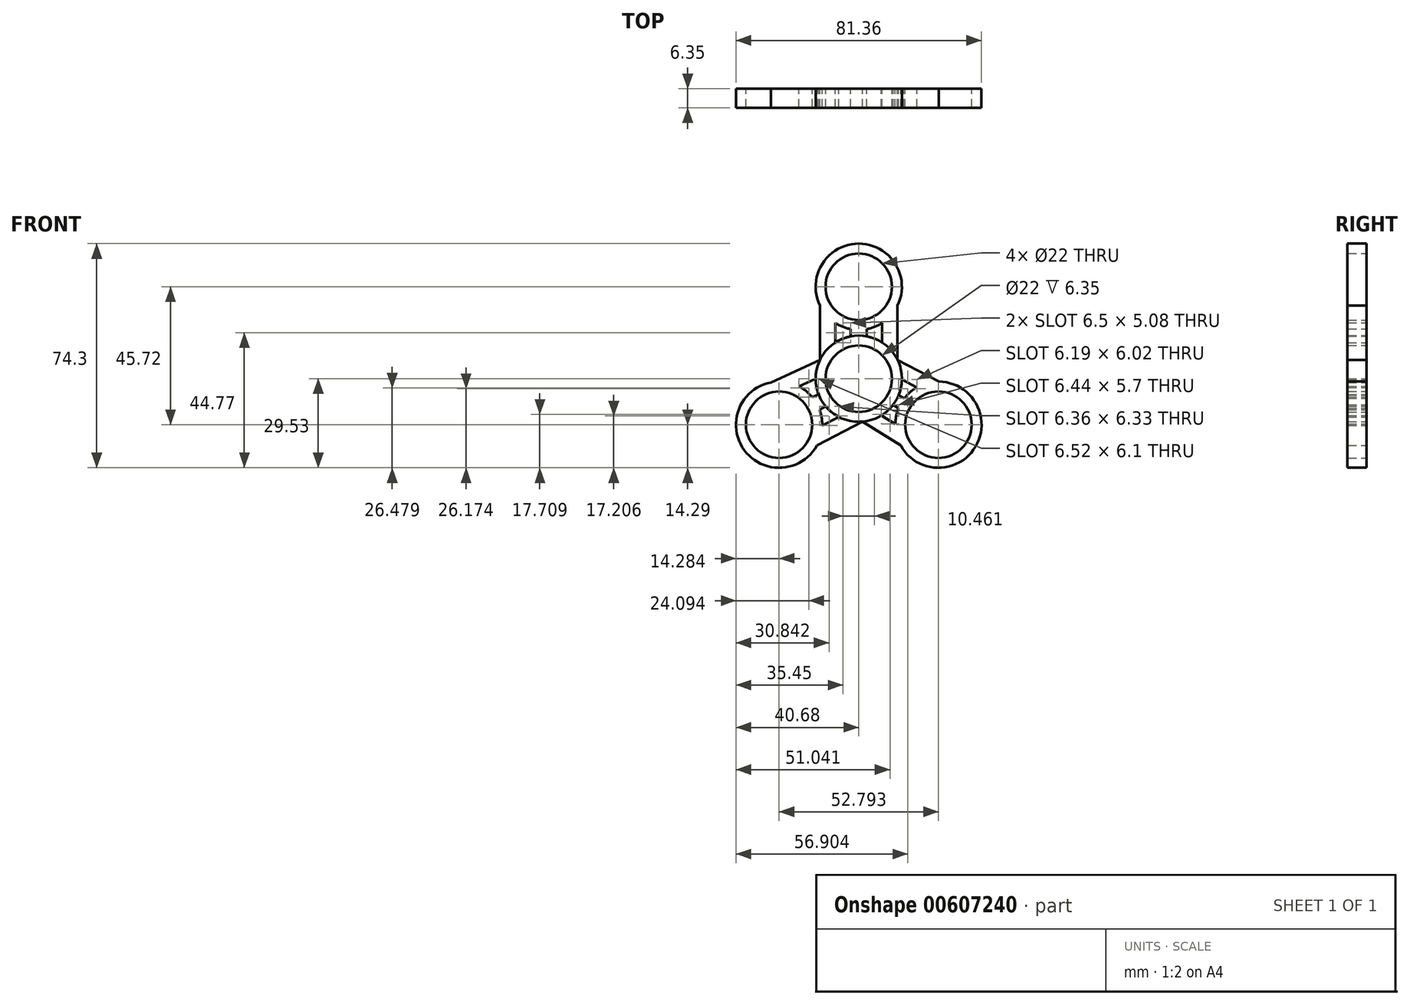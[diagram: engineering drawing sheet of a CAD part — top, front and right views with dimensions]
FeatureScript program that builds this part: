
annotation { "Feature Type Name" : "Feature", "Feature Type Description" : "" }
export const myFeature = defineFeature(function(context is Context, id is Id, definition is map)
    precondition{}
    {
        {
            var Q0;
            Q0=qCreatedBy(makeId("Front.planeOp"),FACE);
            var sketch = newSketch(context, id + "F0", { "sketchPlane" : qUnion([Q0])});
            skCircle(sketch, "E0", {"center": v(0, 0) * mm, "radius": 14.29 * mm});
            skCircle(sketch, "E1", {"center": v(0, 0) * mm, "radius": 11 * mm});
            skCircle(sketch, "E2", {"center": v(0, 30.48) * mm, "radius": 14.29 * mm});
            skCircle(sketch, "E3", {"center": v(0, 30.48) * mm, "radius": 11 * mm});
            skCircle(sketch, "E4.1.2", {"center": v(-26.4, -15.24) * mm, "radius": 11 * mm});
            skCircle(sketch, "E4.1.3", {"center": v(-26.4, -15.24) * mm, "radius": 14.29 * mm});
            skCircle(sketch, "E4.2.2", {"center": v(26.4, -15.24) * mm, "radius": 11 * mm});
            skCircle(sketch, "E4.2.3", {"center": v(26.4, -15.24) * mm, "radius": 14.29 * mm});
            skSolve(sketch);
        }
        {
            var Q0;
            Q0=qCreatedBy(makeId("Front.planeOp"),FACE);
            var sketch = newSketch(context, id + "F1", { "sketchPlane" : qUnion([Q0])});
            skCircle(sketch, "E5.0", {"center": v(0, 30.48) * mm, "radius": 14.29 * mm});
            skCircle(sketch, "E6.0", {"center": v(0, 30.48) * mm, "radius": 11 * mm});
            skCircle(sketch, "E7.0", {"center": v(0, 0) * mm, "radius": 11 * mm});
            skCircle(sketch, "E8.0", {"center": v(0, 0) * mm, "radius": 14.29 * mm});
            skCircle(sketch, "E9.0", {"center": v(26.4, -15.24) * mm, "radius": 11 * mm});
            skCircle(sketch, "E10.0", {"center": v(26.4, -15.24) * mm, "radius": 14.29 * mm});
            skCircle(sketch, "E11.0", {"center": v(-26.4, -15.24) * mm, "radius": 11 * mm});
            skCircle(sketch, "E12.0", {"center": v(-26.4, -15.24) * mm, "radius": 14.29 * mm});
            skLineSegment(sketch, "E13", {"start": v(-12.85, 24.24) * mm, "end": v(-12.85, 6.24) * mm});
            skLineSegment(sketch, "E14", {"start": v(12.85, 24.24) * mm, "end": v(12.85, 6.24) * mm});
            skLineSegment(sketch, "E15", {"start": v(-13.9, -22.15) * mm, "end": v(1.26, -14.23) * mm});
            skLineSegment(sketch, "E16", {"start": v(1.26, -14.23) * mm, "end": v(13.9, -22.15) * mm});
            skLineSegment(sketch, "E17", {"start": v(26.47, -0.95) * mm, "end": v(12.85, 6.24) * mm});
            skLineSegment(sketch, "E18", {"start": v(-12.85, 6.24) * mm, "end": v(-29.16, -1.22) * mm});
            skLineSegment(sketch, "E19", {"start": v(7.77, 11.99) * mm, "end": v(7.77, 18.5) * mm});
            skLineSegment(sketch, "E20", {"start": v(-7.77, 18.5) * mm, "end": v(-7.77, 11.99) * mm});
            skLineSegment(sketch, "E21", {"start": v(-14.29, 0) * mm, "end": v(-19.84, -2.54) * mm});
            skLineSegment(sketch, "E22", {"start": v(-12.11, -15.49) * mm, "end": v(-6.66, -12.64) * mm});
            skLineSegment(sketch, "E23", {"start": v(7.5, -12.16) * mm, "end": v(12.11, -15.04) * mm});
            skLineSegment(sketch, "E24", {"start": v(14.29, -0.26) * mm, "end": v(19.24, -2.88) * mm});
            skLineSegment(sketch, "E25", {"start": v(11.4, -8.6) * mm, "end": v(13.21, -9.73) * mm});
            skLineSegment(sketch, "E26", {"start": v(13.21, -5.44) * mm, "end": v(15.13, -6.45) * mm});
            skLineSegment(sketch, "E27", {"start": v(-13.33, -5.15) * mm, "end": v(-15.41, -6.1) * mm});
            skLineSegment(sketch, "E28", {"start": v(-13.02, -10.23) * mm, "end": v(-10.97, -9.16) * mm});
            skLineSegment(sketch, "E29", {"start": v(-10.97, -9.16) * mm, "end": v(-11.16, -9.28) * mm});
            skLineSegment(sketch, "E30", {"start": v(-2.7, 16.45) * mm, "end": v(-2.7, 14.03) * mm});
            skLineSegment(sketch, "E31", {"start": v(2.7, 16.45) * mm, "end": v(2.7, 14.03) * mm});
            skSolve(sketch);
        }
        {
            var Q0;
            {var subQ0=sQuery(id+"F1.wireOp",EDGE,"E8.0");var subQ1=sQuery(id+"F1.wireOp",EDGE,"E75473pT-KR4w-GPLl-tIWS-s1hwGxaYuD1d");var subQ2=makeQuery(id+"F1.imprint","INTERSECT",VERTEX,{"disambiguationData":[OD(0.0)],"derivedFrom":[subQ1,subQ0]});Q0=makeQuery(id+"F1.imprint","IMPRINT",FACE,{"disambiguationData":[TD([[makeQuery(id+"F1.imprint","IMPRINT",EDGE,{"disambiguationData":[TD([[subQ2,-1.0]])],"derivedFrom":subQ1}),1.0]])]});}
            var Q1;
            {var subQ0=sQuery(id+"F1.wireOp",EDGE,"E8.0");var subQ1=sQuery(id+"F1.wireOp",EDGE,"UQbH4uQf-tco6-kiW7-QBOc-czMYGTiRIqUf");var subQ2=makeQuery(id+"F1.imprint","INTERSECT",VERTEX,{"disambiguationData":[OD(0.0)],"derivedFrom":[subQ1,subQ0]});Q1=makeQuery(id+"F1.imprint","IMPRINT",FACE,{"disambiguationData":[TD([[makeQuery(id+"F1.imprint","IMPRINT",EDGE,{"disambiguationData":[TD([[subQ2,-1.0]])],"derivedFrom":subQ1}),1.0]])]});}
            var Q2;
            {var subQ0=sQuery(id+"F1.wireOp",EDGE,"RHKiTu8T-B7F3-O5vr-oPhw-GQMkx3ZWOzNJ");var subQ1=sQuery(id+"F1.wireOp",EDGE,"E5.0");var subQ2=makeQuery(id+"F1.imprint","INTERSECT",VERTEX,{"disambiguationData":[OD(0.0)],"derivedFrom":[subQ1,subQ0]});Q2=makeQuery(id+"F1.imprint","IMPRINT",FACE,{"disambiguationData":[TD([[makeQuery(id+"F1.imprint","IMPRINT",EDGE,{"disambiguationData":[TD([[subQ2,1.0]])],"derivedFrom":subQ1}),1.0]])]});}
            var Q3;
            {var subQ0=sQuery(id+"F1.wireOp",EDGE,"RHKiTu8T-B7F3-O5vr-oPhw-GQMkx3ZWOzNJ");var subQ1=sQuery(id+"F1.wireOp",EDGE,"E10.0");var subQ2=makeQuery(id+"F1.imprint","INTERSECT",VERTEX,{"disambiguationData":[OD(0.0)],"derivedFrom":[subQ1,subQ0]});Q3=makeQuery(id+"F1.imprint","IMPRINT",FACE,{"disambiguationData":[TD([[makeQuery(id+"F1.imprint","IMPRINT",EDGE,{"disambiguationData":[TD([[subQ2,-1.0]])],"derivedFrom":subQ1}),1.0]])]});}
            var Q4;
            Q4=makeQuery(id+"F1.imprint","IMPRINT",FACE,{"disambiguationData":[TD([[makeQuery(id+"F1.imprint","IMPRINT",EDGE,{"derivedFrom":sQuery(id+"F1.wireOp",EDGE,"E11.0")}),-1.0]])]});
            var Q5;
            Q5=makeQuery(id+"F1.imprint","IMPRINT",FACE,{"disambiguationData":[TD([[makeQuery(id+"F1.imprint","IMPRINT",EDGE,{"derivedFrom":sQuery(id+"F1.wireOp",EDGE,"E6.0")}),-1.0]])]});
            var Q6;
            Q6=makeQuery(id+"F1.imprint","IMPRINT",FACE,{"disambiguationData":[TD([[makeQuery(id+"F1.imprint","IMPRINT",EDGE,{"derivedFrom":sQuery(id+"F1.wireOp",EDGE,"E9.0")}),-1.0]])]});
            var Q7;
            Q7=makeQuery(id+"F1.imprint","IMPRINT",FACE,{"disambiguationData":[TD([[makeQuery(id+"F1.imprint","IMPRINT",EDGE,{"derivedFrom":sQuery(id+"F1.wireOp",EDGE,"E7.0")}),-1.0]])]});
            var Q8;
            Q8=makeQuery(id+"F0.imprint","IMPRINT",FACE,{"disambiguationData":[TD([[makeQuery(id+"F0.imprint","IMPRINT",EDGE,{"derivedFrom":sQuery(id+"F0.wireOp",EDGE,"E1")}),-1.0]])]});
            var Q9;
            {var subQ0=sQuery(id+"F1.wireOp",EDGE,"E13");Q9=makeQuery(id+"F1.imprint","IMPRINT",FACE,{"disambiguationData":[TD([[makeQuery(id+"F1.imprint","IMPRINT",EDGE,{"derivedFrom":subQ0}),1.0]])]});}
            var Q10;
            {var subQ0=sQuery(id+"F1.wireOp",EDGE,"E14");Q10=makeQuery(id+"F1.imprint","IMPRINT",FACE,{"disambiguationData":[TD([[makeQuery(id+"F1.imprint","IMPRINT",EDGE,{"derivedFrom":subQ0}),-1.0]])]});}
            var Q11;
            {var subQ0=sQuery(id+"F1.wireOp",EDGE,"E23");Q11=makeQuery(id+"F1.imprint","IMPRINT",FACE,{"disambiguationData":[TD([[makeQuery(id+"F1.imprint","IMPRINT",EDGE,{"derivedFrom":subQ0}),-1.0]])]});}
            var Q12;
            {var subQ0=sQuery(id+"F1.wireOp",EDGE,"E22");Q12=makeQuery(id+"F1.imprint","IMPRINT",FACE,{"disambiguationData":[TD([[makeQuery(id+"F1.imprint","IMPRINT",EDGE,{"derivedFrom":subQ0}),-1.0]])]});}
            var Q13;
            {var subQ0=sQuery(id+"F1.wireOp",EDGE,"E18");Q13=makeQuery(id+"F1.imprint","IMPRINT",FACE,{"disambiguationData":[TD([[makeQuery(id+"F1.imprint","IMPRINT",EDGE,{"derivedFrom":subQ0}),1.0]])]});}
            var Q14;
            {var subQ0=sQuery(id+"F1.wireOp",EDGE,"E27");Q14=makeQuery(id+"F1.imprint","IMPRINT",FACE,{"disambiguationData":[TD([[makeQuery(id+"F1.imprint","IMPRINT",EDGE,{"derivedFrom":subQ0}),1.0]])]});}
            var Q15;
            {var subQ0=sQuery(id+"F1.wireOp",EDGE,"E30");Q15=makeQuery(id+"F1.imprint","IMPRINT",FACE,{"disambiguationData":[TD([[makeQuery(id+"F1.imprint","IMPRINT",EDGE,{"derivedFrom":subQ0}),1.0]])]});}
            var Q16;
            {var subQ0=sQuery(id+"F1.wireOp",EDGE,"E24");Q16=makeQuery(id+"F1.imprint","IMPRINT",FACE,{"disambiguationData":[TD([[makeQuery(id+"F1.imprint","IMPRINT",EDGE,{"derivedFrom":subQ0}),1.0]])]});}
            var Q17;
            {var subQ0=sQuery(id+"F1.wireOp",EDGE,"E25");Q17=makeQuery(id+"F1.imprint","IMPRINT",FACE,{"disambiguationData":[TD([[makeQuery(id+"F1.imprint","IMPRINT",EDGE,{"derivedFrom":subQ0}),1.0]])]});}
            extrude(context, id + "F2", {"entities" : qUnion([Q0, Q1, Q2, Q3, Q4, Q5, Q6, Q7, Q8, Q9, Q10, Q11, Q12, Q13, Q14, Q15, Q16, Q17]), "depth" : 6.35 * mm, "offsetDistance" : 25.4 * mm});
        }
    });
